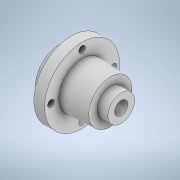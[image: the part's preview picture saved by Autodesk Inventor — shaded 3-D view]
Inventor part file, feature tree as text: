
AUTODESK INVENTOR PART (.ipt)
format: ipt  version: 2021 (Build 250183000, 183)  size: 163,328 bytes
history: native  units: mm
features: sketch x2, revolve x1, extrude x1
ambient origin geometry x8: Origin, YZ Plane, XZ Plane, XY Plane, X Axis, Y Axis, Z Axis, Center Point
bodies: Solid1 (feature_tree)
feature tree (4):
  revolve  "Revolution1"  [1 undecoded]
  extrude  "Extrusion1"  Depth=15.0mm
  sketch  "Sketch1"  dims[d0=75.0mm d1=54.0mm]
  sketch  "Sketch2"  dims[d2=22.0mm d3=15.0mm d4=17.0mm d5=13.0mm d6=28.0mm d7=13.0mm d8=12.0mm d9=8.0mm d10=13.0mm d11=16.0mm d12=26.0mm d13=15.0mm d14=54.0mm d15=62.0mm d16=90.0deg d19=8.0mm d20=37.5mm d21=40.0mm d23=360.0deg d25=10.0mm d26=0.0mm]
note: 1 required parameter value undecoded (feature->parameter linkage not recoverable at this tier; creation-order binding heuristic only, values carry confidence <= 0.55)
